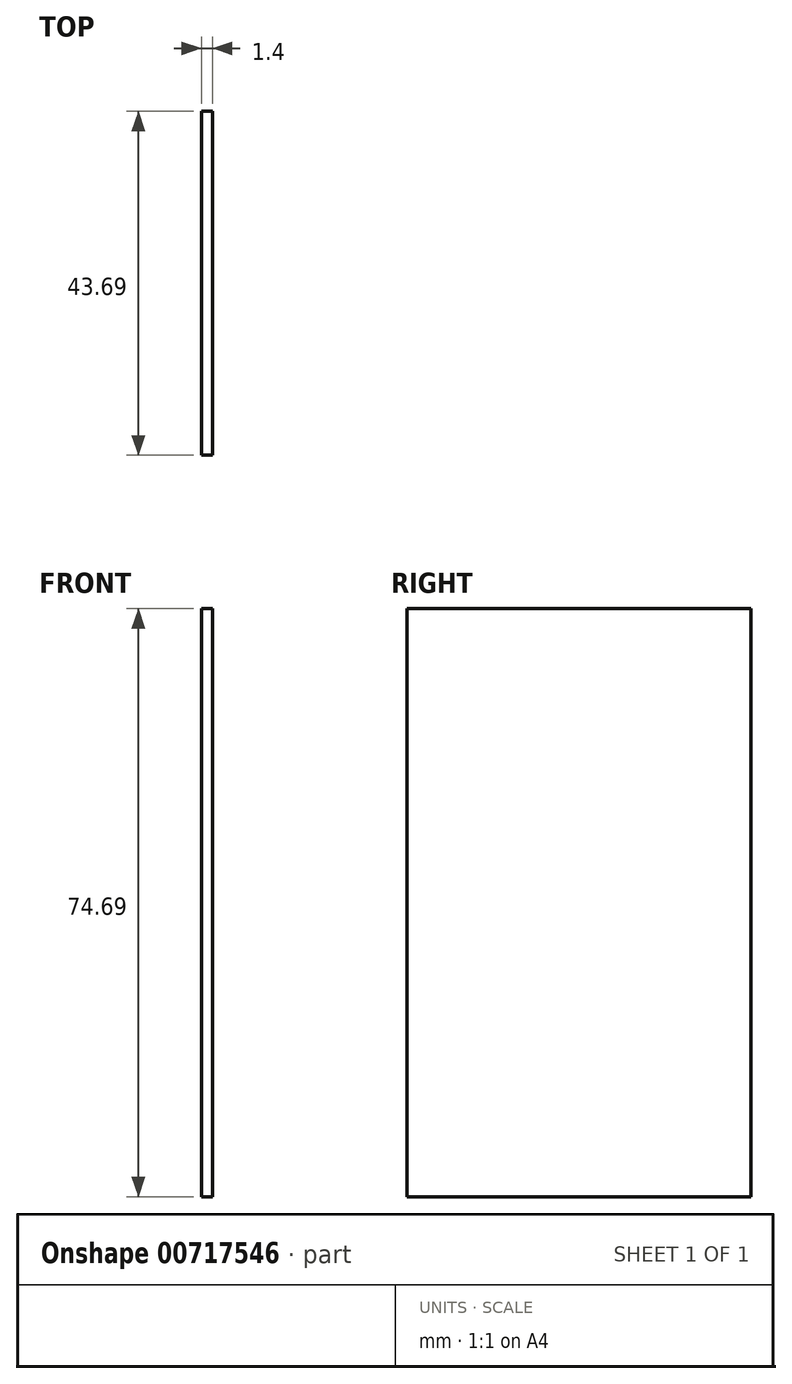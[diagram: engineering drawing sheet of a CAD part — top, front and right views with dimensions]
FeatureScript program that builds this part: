
annotation { "Feature Type Name" : "Feature", "Feature Type Description" : "" }
export const myFeature = defineFeature(function(context is Context, id is Id, definition is map)
    precondition{}
    {
        {
            var Q0;
            Q0=qCreatedBy(makeId("Front.planeOp"),FACE);
            var sketch = newSketch(context, id + "F0", { "sketchPlane" : qUnion([Q0])});
            skLineSegment(sketch, "E0.bottom", {"start": v(-45.18, 44.9) * mm, "end": v(-43.78, 44.9) * mm});
            skLineSegment(sketch, "E0.top", {"start": v(-45.18, -29.8) * mm, "end": v(-43.78, -29.8) * mm});
            skLineSegment(sketch, "E0.left", {"start": v(-45.18, 44.9) * mm, "end": v(-45.18, -29.8) * mm});
            skLineSegment(sketch, "E0.right", {"start": v(-43.78, 44.9) * mm, "end": v(-43.78, -29.8) * mm});
            skSolve(sketch);
        }
        {
            var Q0;
            Q0=makeQuery(id+"F0.imprint","IMPRINT",FACE,{"disambiguationData":[TD([[makeQuery(id+"F0.imprint","IMPRINT",EDGE,{"derivedFrom":sQuery(id+"F0.wireOp",EDGE,"E0.bottom")}),-1.0]])]});
            extrude(context, id + "F1", {"entities" : qUnion([Q0]), "depth" : 43.69 * mm, "offsetDistance" : 25.4 * mm});
        }
    });
